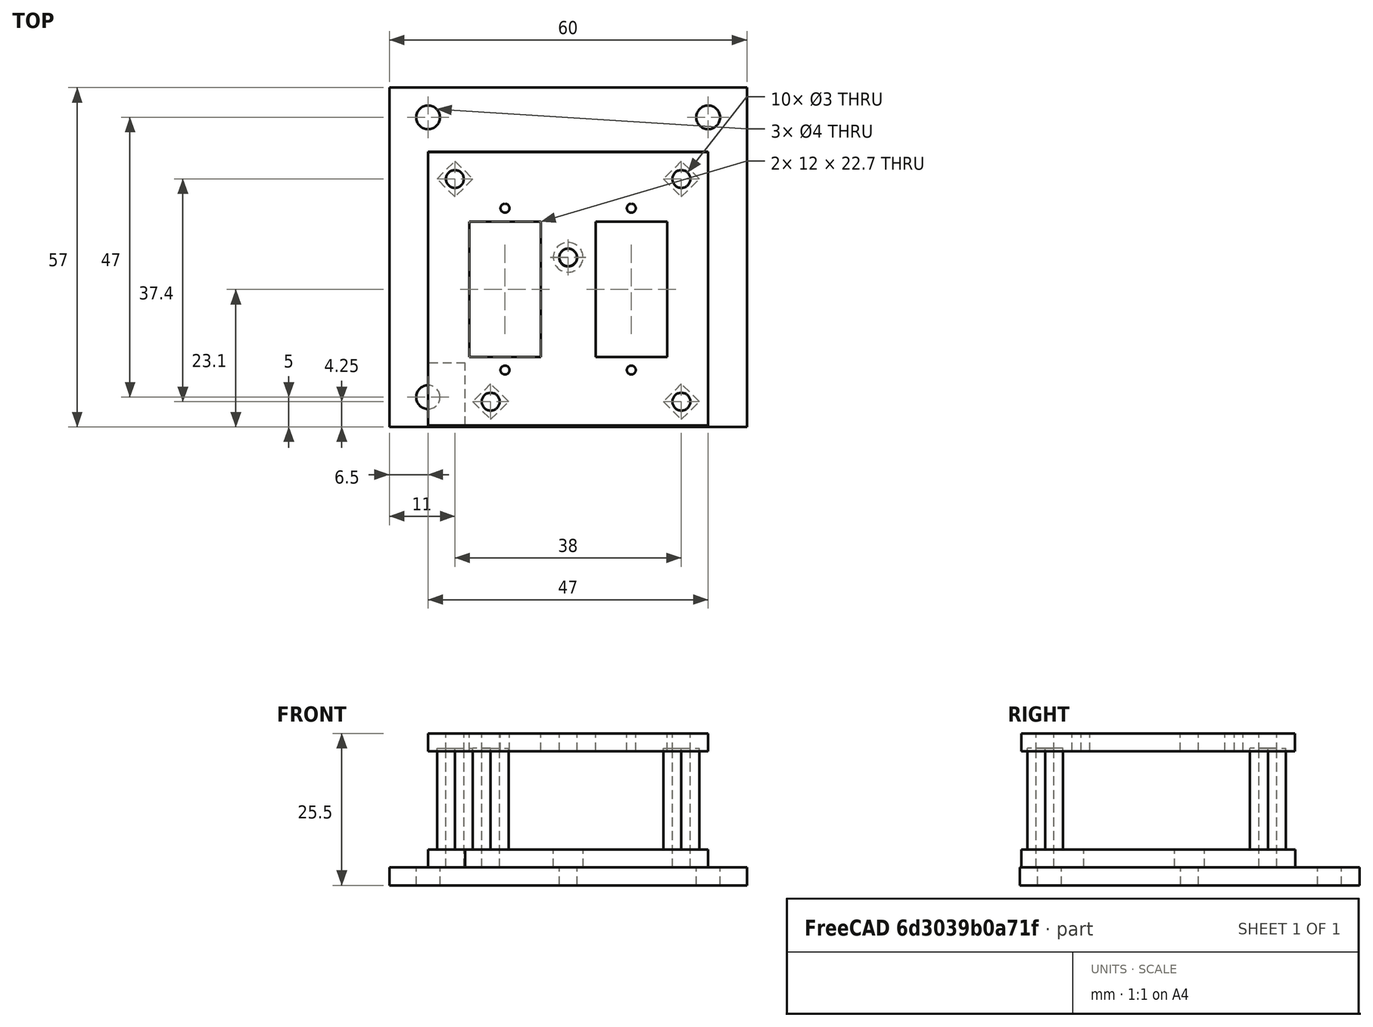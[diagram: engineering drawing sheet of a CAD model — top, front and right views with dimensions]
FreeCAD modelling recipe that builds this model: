
FCSTD DOCUMENT  (FreeCAD 0.17R13541 (Git))
Label: cabin climb gauge
License: All rights reserved
LicenseURL: http://en.wikipedia.org/wiki/All_rights_reserved
objects: Part::Cylinder×14, Part::Cut×12, Part::Box×5, Part::FeaturePython×5, Part::Prism×3, Part::MultiFuse×3, Part::Fuse×2, Part::Mirroring×2
note: 46 computed .brp shape members not serialized (recipe doc carries the construction recipe); baked Part::Feature solids carry a one-line shape summary decoded from their .brp

FEATURE [Part::Box] Box  label="cabin climb plate"
  AttacherType = Attacher::AttachEngine3D
  Height = 3
  Length = 60
  Width = 57
FEATURE [Part::Cylinder] Cylinder  label="taladro 1"
  Angle = 360
  AttacherType = Attacher::AttachEngine3D
  Height = 10
  Placement = pos=(6.5,5,0) rot=(0,0,1;0rad)
  Radius = 2
FEATURE [Part::Cylinder] Cylinder001  label="taladro 2"
  Angle = 360
  AttacherType = Attacher::AttachEngine3D
  Height = 10
  Placement = pos=(6.5,52,0) rot=(0,0,1;0rad)
  Radius = 2
FEATURE [Part::Cylinder] Cylinder002  label="taladro 3"
  Angle = 360
  AttacherType = Attacher::AttachEngine3D
  Height = 10
  Placement = pos=(53.5,52,0) rot=(0,0,1;0rad)
  Radius = 2
FEATURE [Part::Cylinder] Cylinder003  label="taladro 4"
  Angle = 360
  AttacherType = Attacher::AttachEngine3D
  Height = 10
  Placement = pos=(30,28.5,0) rot=(0,0,1;0rad)
  Radius = 1.5
FEATURE [Part::Cut] Cut
  Base = -> Box
  Refine = true
  Tool = -> Cylinder
FEATURE [Part::Cut] Cut001
  Base = -> Cut
  Refine = true
  Tool = -> Cylinder001
FEATURE [Part::Cut] Cut002
  Base = -> Cut001
  Refine = true
  Tool = -> Cylinder002
FEATURE [Part::Cut] Cut003  label="plate agujereada"
  Base = -> Cut002
  Refine = true
  Tool = -> Cylinder003
FEATURE [Part::Box] Box001  label="top plate 2"
  AttacherType = Attacher::AttachEngine3D
  Height = 3
  Length = 47
  Placement = pos=(3.25,-1.5,3) rot=(0,0,1;0rad)
  Width = 46
FEATURE [Part::Cylinder] Cylinder004  label="taladro 005"
  Angle = 360
  AttacherType = Attacher::AttachEngine3D
  Height = 10
  Placement = pos=(26.75,26.75,0) rot=(0,0,1;0rad)
  Radius = 2.5
FEATURE [Part::Cylinder] Cylinder005  label="taladro 006"
  Angle = 360
  AttacherType = Attacher::AttachEngine3D
  Height = 27
  Placement = pos=(7.75,2.5,0) rot=(0,0,1;0rad)
  Radius = 1.5
FEATURE [Part::Box] Box002  label="base 2"
  AttacherType = Attacher::AttachEngine3D
  Height = 3
  Length = 47
  Placement = pos=(3.25,-1.5,22.5) rot=(0,0,1;0rad)
  Width = 45.9
FEATURE [Part::Box] Box003  label="Taladro servomotor"
  AttacherType = Attacher::AttachEngine3D
  Height = 10
  Length = 12
  Placement = pos=(10.15,10,19.5) rot=(0,0,1;0rad)
  Width = 22.7
FEATURE [Part::Cylinder] Cylinder006  label="taladro 5"
  Angle = 360
  AttacherType = Attacher::AttachEngine3D
  Height = 10
  Placement = pos=(7.75,2.5,19.5) rot=(0,0,1;0rad)
  Radius = 1.5
FEATURE [Part::Cylinder] Cylinder007  label="Taladro 6"
  Angle = 360
  AttacherType = Attacher::AttachEngine3D
  Height = 10
  Placement = pos=(26.75,26.7,19.5) rot=(0,0,1;0rad)
  Radius = 1.5
FEATURE [Part::Cylinder] Cylinder008  label="Taladro 7"
  Angle = 360
  AttacherType = Attacher::AttachEngine3D
  Height = 10
  Placement = pos=(16.15,7.8,19.5) rot=(0,0,1;0rad)
  Radius = 0.75
FEATURE [Part::Cylinder] Cylinder009  label="taladro adicional 3"
  Angle = 360
  AttacherType = Attacher::AttachEngine3D
  Height = 27
  Placement = pos=(45.75,39.9,0) rot=(0,0,1;0rad)
  Radius = 1.5
FEATURE [Part::Box] Box004  label="Recorte placa"
  AttacherType = Attacher::AttachEngine3D
  Height = 3
  Length = 10
  Placement = pos=(44,-2,3) rot=(0,0,1;0rad)
  Width = 11
FEATURE [Part::Prism] Prism  label="Columna"
  AttacherType = Attacher::AttachEngine3D
  Circumradius = 3
  Height = 20
  Placement = pos=(7.75,2.5,3) rot=(0,0,1;0rad)
  Polygon = 4
FEATURE [Part::FeaturePython] Array002  label="Array taladro 4"  # Draft array (typed FeaturePython)
  Angle = 360
  ArrayType = 0
  Axis = (0,0,1)
  Base = -> Cylinder005
  Center = (0,0,0)
  Fuse = false
  IntervalAxis = (0,0,0)
  IntervalX = (38,0,0)
  IntervalY = (0,37.4,0)
  IntervalZ = (0,0,0)
  NumberPolar = 1
  NumberX = 1
  NumberY = 2
  NumberZ = 1
FEATURE [Part::Fuse] Fusion002  label="Taladros 2"
  Base = -> Cylinder004
  Refine = true
  Tool = -> Array002
FEATURE [Part::FeaturePython] Array003  label="Array columnas"  # Draft array (typed FeaturePython)
  Angle = 360
  ArrayType = 0
  Axis = (0,0,1)
  Base = -> Prism
  Center = (0,0,0)
  Fuse = false
  IntervalAxis = (0,0,0)
  IntervalX = (38,0,0)
  IntervalY = (0,37.4,0)
  IntervalZ = (0,0,0)
  NumberPolar = 1
  NumberX = 1
  NumberY = 2
  NumberZ = 1
FEATURE [Part::Fuse] Fusion001  label="top plate columnas"
  Base = -> Box001
  Refine = true
  Tool = -> Array003
FEATURE [Part::Cut] Cut004  label="Top plate"
  Base = -> Fusion001
  Refine = true
  Tool = -> Fusion002
FEATURE [Part::FeaturePython] Array004  label="Array taladro servomotor"  # Draft array (typed FeaturePython)
  Angle = 360
  ArrayType = 0
  Axis = (0,0,1)
  Base = -> Box003
  Center = (0,0,0)
  Fuse = false
  IntervalAxis = (0,0,0)
  IntervalX = (21.2,0,0)
  IntervalY = (0,1,0)
  IntervalZ = (0,0,0)
  NumberPolar = 1
  NumberX = 2
  NumberY = 1
  NumberZ = 1
FEATURE [Part::FeaturePython] Array005  label="Array taladro 5"  # Draft array (typed FeaturePython)
  Angle = 360
  ArrayType = 0
  Axis = (0,0,1)
  Base = -> Cylinder006
  Center = (0,0,0)
  Fuse = false
  IntervalAxis = (0,0,0)
  IntervalX = (38,0,0)
  IntervalY = (0,37.4,0)
  IntervalZ = (0,0,0)
  NumberPolar = 1
  NumberX = 1
  NumberY = 2
  NumberZ = 1
FEATURE [Part::FeaturePython] Array006  label="Array taladros 7"  # Draft array (typed FeaturePython)
  Angle = 360
  ArrayType = 0
  Axis = (0,0,1)
  Base = -> Cylinder008
  Center = (0,0,0)
  Fuse = false
  IntervalAxis = (0,0,0)
  IntervalX = (21.2,0,0)
  IntervalY = (0,27.2,0)
  IntervalZ = (0,0,0)
  NumberPolar = 1
  NumberX = 2
  NumberY = 2
  NumberZ = 1
FEATURE [Part::MultiFuse] Fusion003  label="Taladros 3"
  Refine = true
  Shapes = -> [Cylinder007,Array006,Array004,Array005]
FEATURE [Part::Prism] Prism001  label="Columna 3"
  AttacherType = Attacher::AttachEngine3D
  Circumradius = 3
  Height = 20
  Placement = pos=(45.75,39.9,3) rot=(0,0,1;0rad)
  Polygon = 4
FEATURE [Part::MultiFuse] Fusion004  label="placa con tres taladros"
  Refine = true
  Shapes = -> [Cut004,Prism001]
FEATURE [Part::Prism] Prism002  label="Columna 4"
  AttacherType = Attacher::AttachEngine3D
  Circumradius = 3
  Height = 20
  Placement = pos=(39.75,2.5,3) rot=(0,0,1;0rad)
  Polygon = 4
FEATURE [Part::Cut] Cut005  label="base previa"
  Base = -> Box002
  Refine = true
  Tool = -> Fusion003
FEATURE [Part::Cut] Cut006  label="Placa con tres columnas"
  Base = -> Fusion004
  Refine = true
  Tool = -> Cylinder009
FEATURE [Part::Cut] Cut007  label="Placa tres columnas y tornillo"
  Base = -> Cut006
  Refine = true
  Tool = -> Box004
FEATURE [Part::Cylinder] Cylinder010  label="taladro adicional 4"
  Angle = 360
  AttacherType = Attacher::AttachEngine3D
  Height = 27
  Placement = pos=(39.75,2.5,0) rot=(0,0,1;0rad)
  Radius = 1.5
FEATURE [Part::Cut] Cut008
  Base = -> Cut007
  Refine = true
  Tool = -> Cylinder010
FEATURE [Part::Cylinder] Cylinder011  label="taladro adicional 005"
  Angle = 360
  AttacherType = Attacher::AttachEngine3D
  Height = 27
  Placement = pos=(39.75,2.5,0) rot=(0,0,1;0rad)
  Radius = 1.5
FEATURE [Part::Cut] Cut009
  Base = -> Prism002
  Refine = true
  Tool = -> Cylinder011
FEATURE [Part::MultiFuse] Fusion005  label="top plate final"
  Refine = true
  Shapes = -> [Cut008,Cut009]
FEATURE [Part::Mirroring] Part__Mirroring  label="top plate final (Mirror #1)"
  Base = (0,0,0)
  Normal = (1,0,0)
  Placement = pos=(56.75,1.75,0) rot=(0,0,1;0rad)
  Source = -> Fusion005
FEATURE [Part::Cylinder] Cylinder012  label="taladro 007"
  Angle = 360
  AttacherType = Attacher::AttachEngine3D
  Height = 10
  Placement = pos=(45.75,39.9,19.5) rot=(0,0,1;0rad)
  Radius = 1.5
FEATURE [Part::Cut] Cut010  label="base 3 taladros"
  Base = -> Cut005
  Refine = true
  Tool = -> Cylinder012
FEATURE [Part::Cylinder] Cylinder013  label="taladro 008"
  Angle = 360
  AttacherType = Attacher::AttachEngine3D
  Height = 10
  Placement = pos=(39.75,2.5,18.5) rot=(0,0,1;0rad)
  Radius = 1.5
FEATURE [Part::Cut] Cut011  label="base final"
  Base = -> Cut010
  Refine = true
  Tool = -> Cylinder013
FEATURE [Part::Mirroring] Part__Mirroring001  label="base final (Mirror #2)"
  Base = (0,0,0)
  Normal = (1,0,0)
  Placement = pos=(56.75,1.75,0) rot=(0,0,1;0rad)
  Source = -> Cut011
